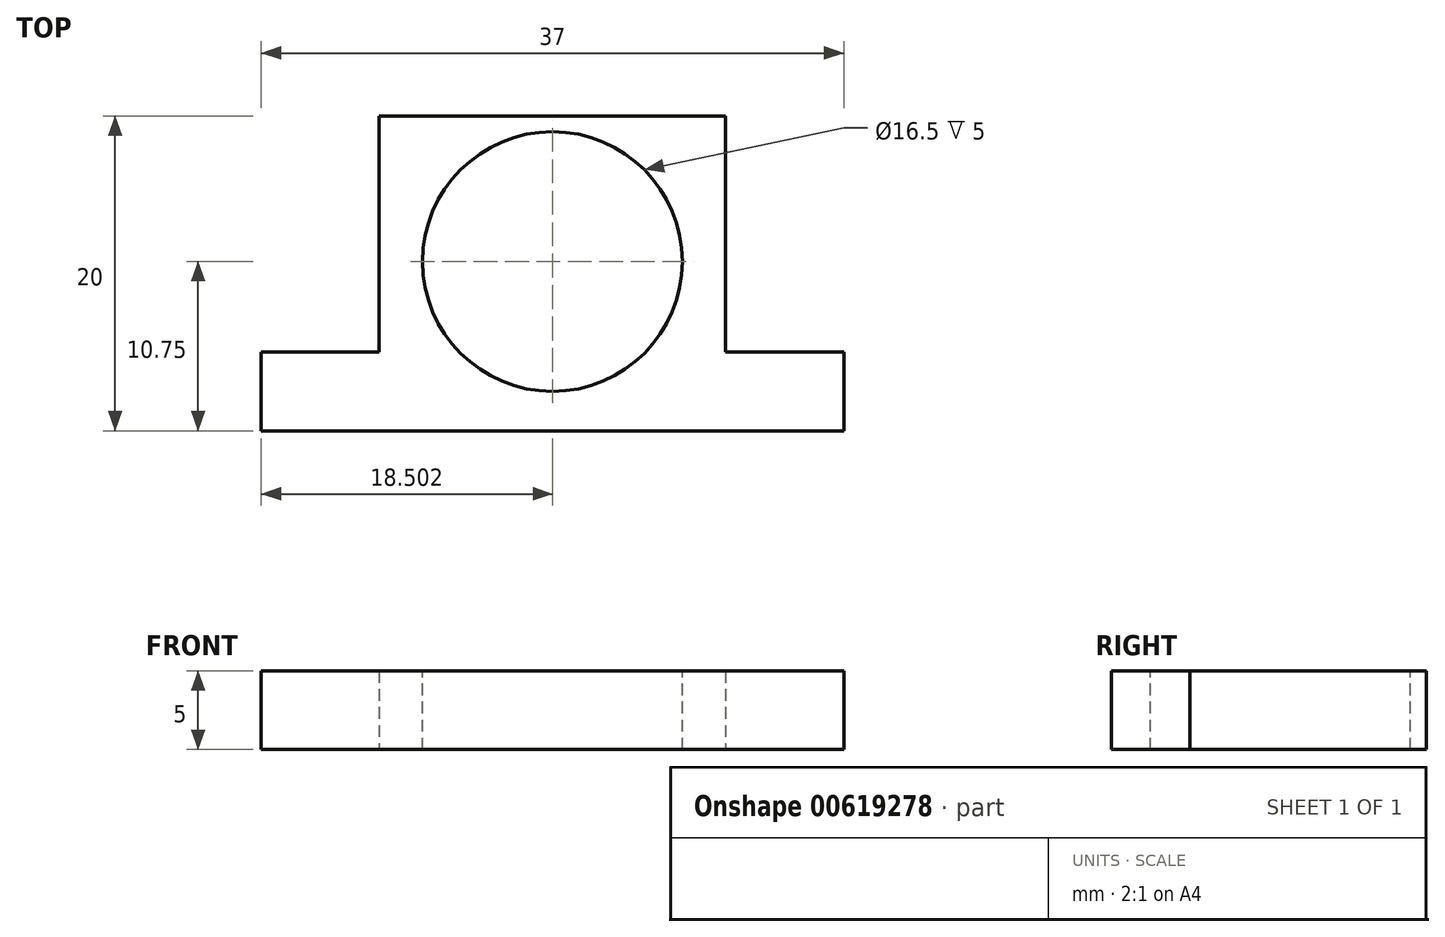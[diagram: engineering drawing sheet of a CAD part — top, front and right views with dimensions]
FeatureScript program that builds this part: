
annotation { "Feature Type Name" : "Feature", "Feature Type Description" : "" }
export const myFeature = defineFeature(function(context is Context, id is Id, definition is map)
    precondition{}
    {
        {
            var Q0;
            Q0=qCreatedBy(makeId("Top.planeOp"),FACE);
            var sketch = newSketch(context, id + "F0", { "sketchPlane" : qUnion([Q0])});
            skLineSegment(sketch, "E0.bottom", {"start": v(-2.47, 0) * mm, "end": v(34.53, 0) * mm});
            skLineSegment(sketch, "E0.top", {"start": v(-2.47, -5) * mm, "end": v(34.53, -5) * mm});
            skLineSegment(sketch, "E0.left", {"start": v(-2.47, 0) * mm, "end": v(-2.47, -5) * mm});
            skLineSegment(sketch, "E0.right", {"start": v(34.53, 0) * mm, "end": v(34.53, -5) * mm});
            skSolve(sketch);
        }
        {
            var Q0;
            Q0 = qSketchRegion(id + "F0", true);
            extrude(context, id + "F1", {"entities" : qUnion([Q0]), "depth" : 5 * mm, "offsetDistance" : 25.4 * mm});
        }
        {
            var Q0;
            Q0=makeQuery(id+"F1.opExtrude","SWEPT_FACE",FACE,{"disambiguationData":[OSD([sQuery(id+"F0.wireOp",EDGE,"E0.bottom")])]});
            var sketch = newSketch(context, id + "F2", { "sketchPlane" : qUnion([Q0])});
            skLineSegment(sketch, "E1.bottom", {"start": v(-27.03, 5) * mm, "end": v(-5.03, 5) * mm});
            skLineSegment(sketch, "E1.top", {"start": v(-27.03, 0) * mm, "end": v(-5.03, 0) * mm});
            skLineSegment(sketch, "E1.left", {"start": v(-27.03, 5) * mm, "end": v(-27.03, 0) * mm});
            skLineSegment(sketch, "E1.right", {"start": v(-5.03, 5) * mm, "end": v(-5.03, 0) * mm});
            skSolve(sketch);
        }
        {
            var Q0;
            Q0 = qSketchRegion(id + "F2", true);
            extrude(context, id + "F3", {"entities" : qUnion([Q0]), "operationType" : NewBodyOperationType.ADD, "depth" : 15 * mm, "offsetDistance" : 25.4 * mm});
        }
        {
            var Q0;
            Q0=makeQuery(id+"F3.opExtrude","SWEPT_FACE",FACE,{"disambiguationData":[OSD([sQuery(id+"F2.wireOp",EDGE,"E1.bottom")])]});
            var sketch = newSketch(context, id + "F4", { "sketchPlane" : qUnion([Q0])});
            skCircle(sketch, "E2", {"center": v(16.03, 5.75) * mm, "radius": 8.25 * mm});
            skSolve(sketch);
        }
        {
            var Q0;
            Q0 = qSketchRegion(id + "F4", true);
            extrude(context, id + "F5", {"entities" : qUnion([Q0]), "operationType" : NewBodyOperationType.REMOVE, "oppositeDirection" : true, "depth" : 25.4 * mm, "offsetDistance" : 25.4 * mm});
        }
    });
